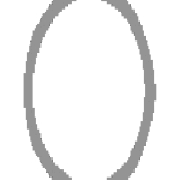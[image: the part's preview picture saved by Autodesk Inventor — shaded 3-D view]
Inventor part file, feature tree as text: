
AUTODESK INVENTOR PART (.ipt)
format: ipt  version: 2021 (Build 250183000, 183)  size: 111,616 bytes
history: native  units: in
note: dims shown in document units (in); Inventor stores cm internally (conversion verified against a paired STEP export)
features: other x4, sketch x3, plane x1
ambient origin geometry x8: Origin, YZ Plane, XZ Plane, XY Plane, X Axis, Y Axis, Z Axis, Center Point
bodies: Solid1 (feature_tree), Body (feature_tree)
feature tree (8):
  other  "Driven Length"
  other  "Frame Generator"
  other  "Start Plane"
  other  "End Plane"
  sketch  "Sketch"  dims[d2=31.4083in d4=-0.0in d5=31.4083in d6=0.12in d7=0.0in d8=90.0deg d9=31.4083in]
  sketch  "Sketch2"  dims[d0=1.0in]
  plane  "Work Plane3"
  sketch  "Sketch3"  dims[d1=0.065in]
